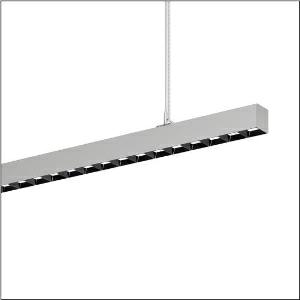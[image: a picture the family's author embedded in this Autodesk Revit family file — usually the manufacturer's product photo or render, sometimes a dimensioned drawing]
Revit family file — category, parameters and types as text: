
# Revit family: silica_r__21_51mx31dc3dsb_b806
name_source: partatom
category: Lighting Fixtures
units: mm (PartAtom-declared; Revit-internal decimal feet)

## family parameters
Cut with Voids When Loaded = No
Host = Face
Light Source = No
Part Type = Normal
Room Calculation Point = No
Round Connector Dimension = Use Diameter
Shared = No

## types (1)
- --- (1 x LED, 18230 lm, 113.3 W, 3000K)
    Apparent Load = 113 VA
    CIE Flux Codes = 87 99 100 59 100
    Color Rendering = 80
    Color Temperature = 3000K
    Default Elevation = 1800 mm
    Description = Silica® 21, office luminaire, primary light control with darklight reflector, of PMMA, black, CAT 2 (L<= 3000cd/m²), light emission: direct/indirect distribution, primary light characteristic: symmetric, installation type: suspended mounting, LED, rated luminous flux: 18.230lm, luminous efficacy: 161lm/W, light colour: 830, colour temperature: 3000K, with terminal, 3+2-pole, max. 2.5mm², mains connection: 220..240V, AC, 50/60Hz, rated input power: 113.3W, luminaire housing, of aluminium, metallic grey (RAL 9006), length: 3.004mm, width: 53mm, height: 53mm, protection rating (complete): IP20, insulation class (complete): insulation class I (protective earthing), certification: CE, permissible operating ambient temperature: 0..+35°C, standard: EN 50419, packaging unit: 1 piece
    Height = 53 mm
    Lamp = 1 x LED
    Lamp Light Flux = 18230 lm
    Lamp Power = 113.3 W
    Lamp count = 1
    Length = 3004 mm
    Luminous efficacy = 161 lm/W
    Manufacturer = Siteco
    ModVariant = No
    Model = 51MX31DC3DSB
    Mounting Place = Ceiling
    Mounting Type = Pendant
    Number of Poles = 1
    OnlyDefault = Yes
    Power Factor = 1
    Product Name = Silica® 21
    Product group = office luminaire | ceiling pendant
    ProductGroupID = 902
    Protection Class = Protection class I
    Protection Degree = IP 20
    RLX_Detail_Level = 1
    RLX_Emergency_Light_Flux = 0 lm
    RLX_Emergency_Type = 0
    RLX_Emergency_Type_DB = No
    RlxData = <blob elided: 65745 chars, md5=efa1c9c9>
    Socket = socket
    Standby Power = 0 W
    System Light Flux = 18230 lm
    System Power = 113 W
    Type Comments = factory setting: luminous flux: 100 % | dim-lin: 254 | 392 mA
    Type Image = l_1297751.jpg
    URL = http://relux.com
    VarID = @adj_051629
    Voltage = 0 V
    Weight = 0.00 kg
    Width = 53 mm

## geometry (parser evidence)
native form markers: Blend x4, Sweep x13
no freeform markers — native parametric forms only
